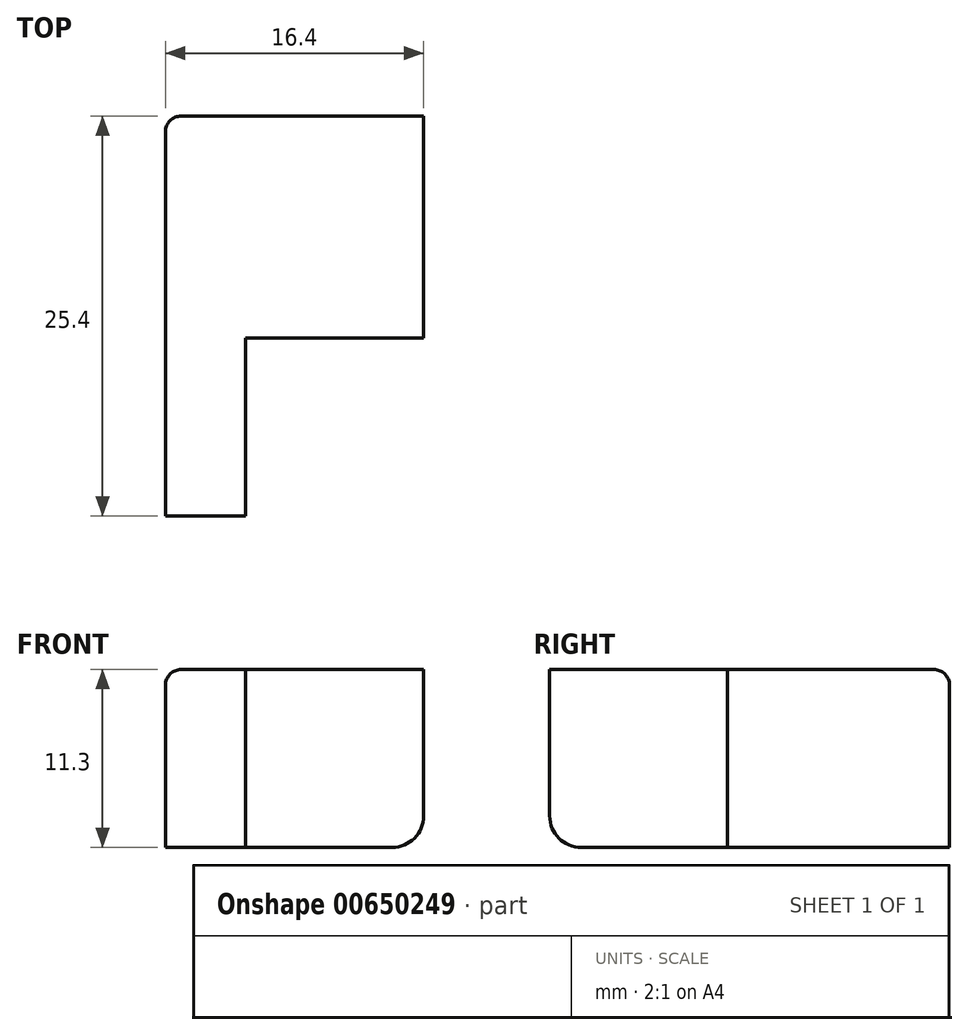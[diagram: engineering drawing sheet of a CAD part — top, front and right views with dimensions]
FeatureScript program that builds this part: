
annotation { "Feature Type Name" : "Feature", "Feature Type Description" : "" }
export const myFeature = defineFeature(function(context is Context, id is Id, definition is map)
    precondition{}
    {
        {
            var Q0;
            Q0=qCreatedBy(makeId("Top.planeOp"),FACE);
            var sketch = newSketch(context, id + "F0", { "sketchPlane" : qUnion([Q0])});
            skLineSegment(sketch, "E0.bottom", {"start": v(0, 0) * mm, "end": v(16.4, 0) * mm});
            skLineSegment(sketch, "E0.top", {"start": v(0, 25.4) * mm, "end": v(16.4, 25.4) * mm});
            skLineSegment(sketch, "E0.left", {"start": v(0, 0) * mm, "end": v(0, 25.4) * mm});
            skLineSegment(sketch, "E0.right", {"start": v(16.4, 0) * mm, "end": v(16.4, 25.4) * mm});
            skSolve(sketch);
        }
        {
            var Q0;
            Q0=makeQuery(id+"F0.imprint","IMPRINT",FACE,{"disambiguationData":[TD([[makeQuery(id+"F0.imprint","IMPRINT",EDGE,{"derivedFrom":sQuery(id+"F0.wireOp",EDGE,"E0.bottom")}),1.0]])]});
            extrude(context, id + "F1", {"entities" : qUnion([Q0]), "depth" : 11.3 * mm, "offsetDistance" : 25 * mm});
        }
        {
            var Q0;
            Q0=makeQuery(id+"F1.opExtrude","CAP_FACE",FACE,{"disambiguationData":[OSD([sQuery(id+"F0.wireOp",EDGE,"E0.bottom"),sQuery(id+"F0.wireOp",EDGE,"E0.top"),sQuery(id+"F0.wireOp",EDGE,"E0.left"),sQuery(id+"F0.wireOp",EDGE,"E0.right")])],"isStart":false});
            var sketch = newSketch(context, id + "F2", { "sketchPlane" : qUnion([Q0])});
            skLineSegment(sketch, "E1.bottom", {"start": v(16.4, 0) * mm, "end": v(5.1, 0) * mm});
            skLineSegment(sketch, "E1.top", {"start": v(16.4, 11.3) * mm, "end": v(5.1, 11.3) * mm});
            skLineSegment(sketch, "E1.left", {"start": v(16.4, 0) * mm, "end": v(16.4, 11.3) * mm});
            skLineSegment(sketch, "E1.right", {"start": v(5.1, 0) * mm, "end": v(5.1, 11.3) * mm});
            skSolve(sketch);
        }
        {
            var Q0;
            Q0=makeQuery(id+"F2.imprint","IMPRINT",FACE,{"disambiguationData":[TD([[makeQuery(id+"F2.imprint","IMPRINT",EDGE,{"derivedFrom":sQuery(id+"F2.wireOp",EDGE,"E1.bottom")}),1.0]])]});
            extrude(context, id + "F3", {"entities" : qUnion([Q0]), "operationType" : NewBodyOperationType.REMOVE, "oppositeDirection" : true, "depth" : 25 * mm, "offsetDistance" : 25 * mm});
        }
        {
            var Q0;
            Q0=makeQuery(id+"F1.opExtrude","CAP_EDGE",EDGE,{"disambiguationData":[OSD([sQuery(id+"F0.wireOp",EDGE,"E0.right")])],"isStart":true});
            var Q1;
            Q1=makeQuery(id+"F1.opExtrude","CAP_EDGE",EDGE,{"disambiguationData":[OSD([sQuery(id+"F0.wireOp",EDGE,"E0.bottom")])],"isStart":true});
            fillet(context, id + "F4", {"entities" : qUnion([Q0, Q1]), "radius" : 2 * mm, "tangentPropagation" : true, "allowEdgeOverflow" : false});
        }
        {
            var Q0;
            Q0=makeQuery(id+"F1.opExtrude","SWEPT_EDGE",EDGE,{"disambiguationData":[OSD([sQuery(id+"F0.wireOp",EDGE,"E0.top"),sQuery(id+"F0.wireOp",EDGE,"E0.left")])]});
            var Q1;
            Q1=makeQuery(id+"F1.opExtrude","CAP_EDGE",EDGE,{"disambiguationData":[OSD([sQuery(id+"F0.wireOp",EDGE,"E0.left")])],"isStart":false});
            var Q2;
            Q2=makeQuery(id+"F1.opExtrude","CAP_EDGE",EDGE,{"disambiguationData":[OSD([sQuery(id+"F0.wireOp",EDGE,"E0.top")])],"isStart":false});
            fillet(context, id + "F5", {"entities" : qUnion([Q0, Q1, Q2]), "radius" : 1 * mm, "tangentPropagation" : true, "allowEdgeOverflow" : false});
        }
    });
